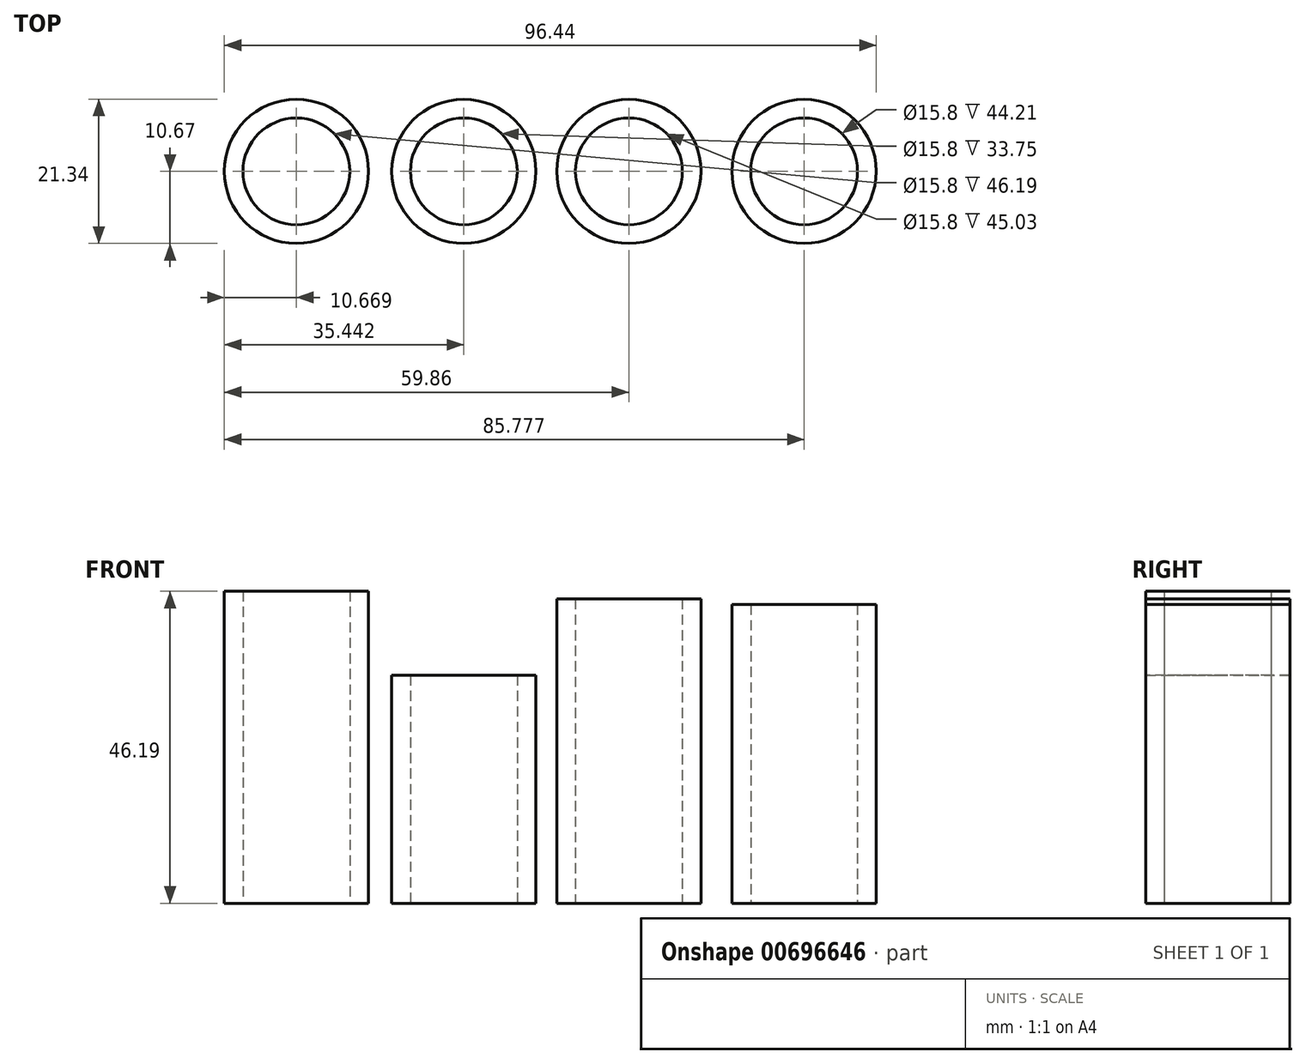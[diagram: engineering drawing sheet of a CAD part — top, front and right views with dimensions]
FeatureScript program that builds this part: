
annotation { "Feature Type Name" : "Feature", "Feature Type Description" : "" }
export const myFeature = defineFeature(function(context is Context, id is Id, definition is map)
    precondition{}
    {
        {
            var Q0;
            Q0=qCreatedBy(makeId("Top.planeOp"),FACE);
            var sketch = newSketch(context, id + "F0", { "sketchPlane" : qUnion([Q0])});
            skCircle(sketch, "E0", {"center": v(0, 0) * mm, "radius": 10.67 * mm});
            skCircle(sketch, "E1", {"center": v(0, 0) * mm, "radius": 7.9 * mm});
            skSolve(sketch);
        }
        {
            var Q0;
            Q0 = qSketchRegion(id + "F0", true);
            extrude(context, id + "F1", {"entities" : qUnion([Q0]), "depth" : 45.03 * mm, "offsetDistance" : 25 * mm});
        }
        {
            var Q0;
            Q0=qCreatedBy(makeId("Top.planeOp"),FACE);
            var sketch = newSketch(context, id + "F2", { "sketchPlane" : qUnion([Q0])});
            skCircle(sketch, "E2", {"center": v(-24.42, 0) * mm, "radius": 10.67 * mm});
            skCircle(sketch, "E3", {"center": v(-24.42, 0) * mm, "radius": 7.9 * mm});
            skSolve(sketch);
        }
        {
            var Q0;
            Q0 = qSketchRegion(id + "F2", true);
            extrude(context, id + "F3", {"entities" : qUnion([Q0]), "depth" : 33.75 * mm, "offsetDistance" : 25 * mm});
        }
        {
            var Q0;
            Q0=qCreatedBy(makeId("Top.planeOp"),FACE);
            var sketch = newSketch(context, id + "F4", { "sketchPlane" : qUnion([Q0])});
            skCircle(sketch, "E4", {"center": v(25.92, 0) * mm, "radius": 10.67 * mm});
            skCircle(sketch, "E5", {"center": v(25.92, 0) * mm, "radius": 7.9 * mm});
            skSolve(sketch);
        }
        {
            var Q0;
            Q0 = qSketchRegion(id + "F4", true);
            extrude(context, id + "F5", {"entities" : qUnion([Q0]), "depth" : 44.2 * mm, "offsetDistance" : 25 * mm});
        }
        {
            var Q0;
            Q0=qCreatedBy(makeId("Top.planeOp"),FACE);
            var sketch = newSketch(context, id + "F6", { "sketchPlane" : qUnion([Q0])});
            skCircle(sketch, "E6", {"center": v(-49.2, 0) * mm, "radius": 10.67 * mm});
            skCircle(sketch, "E7", {"center": v(-49.2, 0) * mm, "radius": 7.9 * mm});
            skSolve(sketch);
        }
        {
            var Q0;
            Q0 = qSketchRegion(id + "F6", true);
            extrude(context, id + "F7", {"entities" : qUnion([Q0]), "depth" : 46.19 * mm, "offsetDistance" : 25 * mm});
        }
    });
